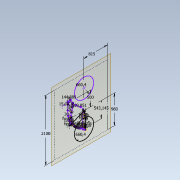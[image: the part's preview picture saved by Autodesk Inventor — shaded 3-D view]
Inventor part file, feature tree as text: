
AUTODESK INVENTOR PART (.ipt)
format: ipt  version: 2021 (Build 250183000, 183)  size: 1,078,784 bytes
history: native  units: mm
features: sketch x3, other x2, plane x1
ambient origin geometry x8: Origin, YZ Plane, XZ Plane, XY Plane, X Axis, Y Axis, Z Axis, Center Point
feature tree (6):
  sketch  "Boceto 3D1"  dims[d3=509.95112mm]
  sketch  "Boceto 3D2"  dims[d100=144.888874mm]
  sketch  "Boceto 3D3"  dims[d154=500.0mm d175=52.5mm d176=52.5mm d177=52.5mm d178=52.5mm d179=52.5mm d180=30.0mm d208=6.0mm d210=52.5mm d211=35.0mm d212=65.0mm d213=52.5mm d214=52.5mm d216=660.4mm d217=660.4mm d234=980.0mm d236=2100.0mm d237=815.0mm d277=70.0mm d369=32.0mm]
  plane  "Plano de trabajo1"
  other  "Punto de trabajo1"
  other  "Imagen2"
